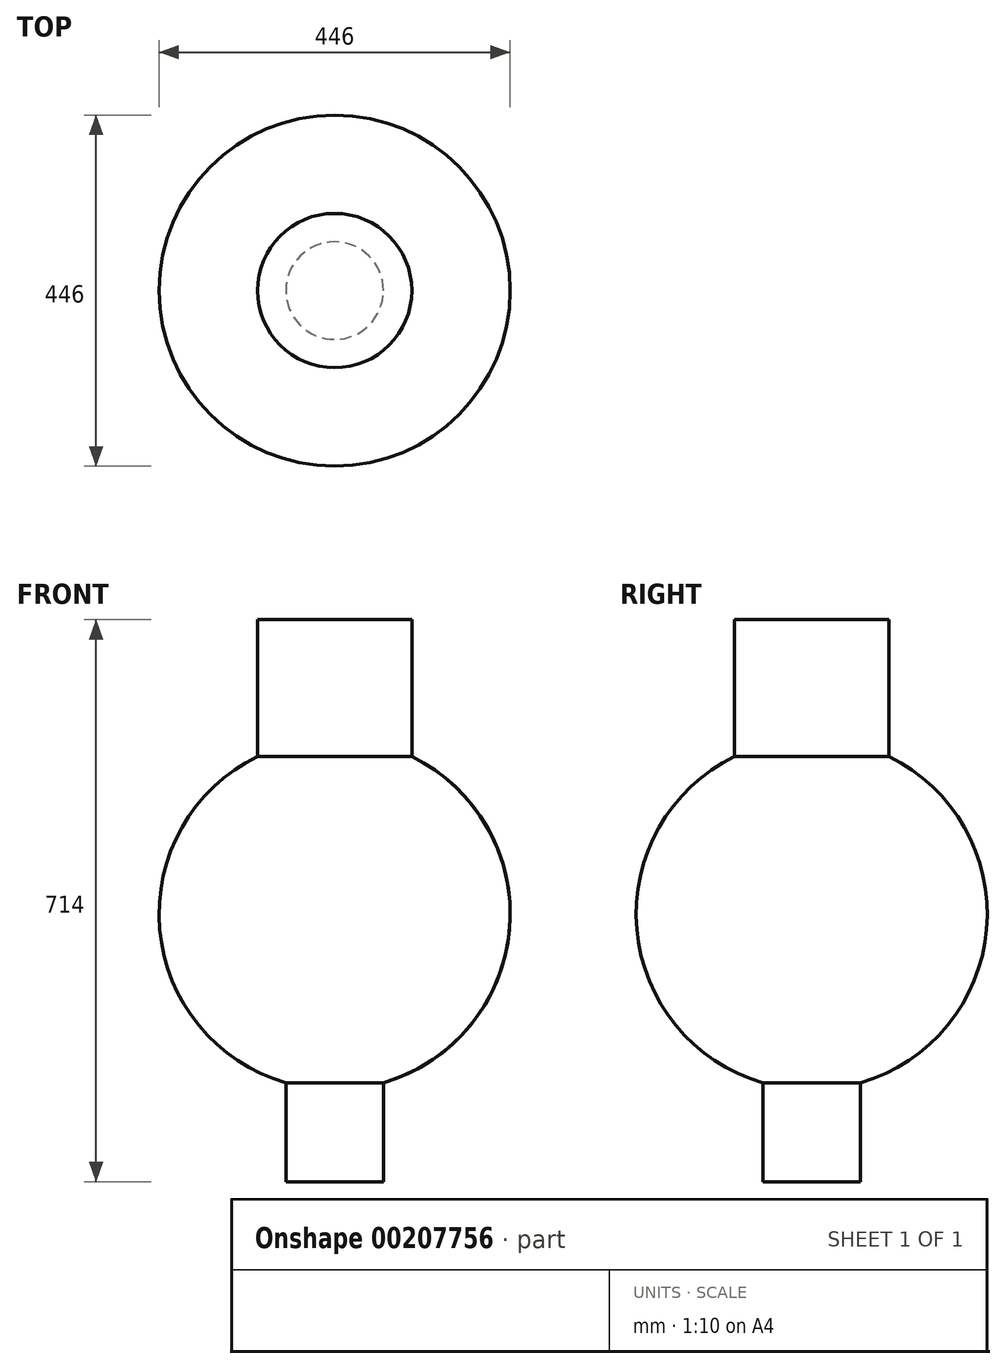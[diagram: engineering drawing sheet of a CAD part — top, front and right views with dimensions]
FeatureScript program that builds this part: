
annotation { "Feature Type Name" : "Feature", "Feature Type Description" : "" }
export const myFeature = defineFeature(function(context is Context, id is Id, definition is map)
    precondition{}
    {
        {
            var Q0;
            Q0=qCreatedBy(makeId("Front.planeOp"),FACE);
            var sketch = newSketch(context, id + "F0", { "sketchPlane" : qUnion([Q0])});
            skLineSegment(sketch, "E0", {"start": v(0, 0) * mm, "end": v(62, 0) * mm});
            skLineSegment(sketch, "E1", {"start": v(62, 0) * mm, "end": v(62, 125.8) * mm});
            skArc(sketch, "E2", {"start": v(62, 125.8) * mm, "mid": v(222.16, 320.7) * mm, "end": v(98, 540.31) * mm});
            skLineSegment(sketch, "E3", {"start": v(98, 540.31) * mm, "end": v(98, 714) * mm});
            skLineSegment(sketch, "E4", {"start": v(98, 714) * mm, "end": v(0, 714) * mm});
            skLineSegment(sketch, "E5", {"start": v(0, 714) * mm, "end": v(0, 0) * mm});
            skSolve(sketch);
        }
        {
            var Q0;
            Q0=makeQuery(id+"F0.imprint","IMPRINT",FACE,{"disambiguationData":[TD([[makeQuery(id+"F0.imprint","IMPRINT",EDGE,{"derivedFrom":sQuery(id+"F0.wireOp",EDGE,"E0")}),1.0]])]});
            var Q1;
            Q1=sQuery(id+"F0.wireOp",EDGE,"E5");
            revolve(context, id + "F1", {"surfaceOperationType" : NewSurfaceOperationType.NEW, "entities" : qUnion([Q0]), "axis" : qUnion([Q1]), "revolveType" : RevolveType.FULL});
        }
    });
